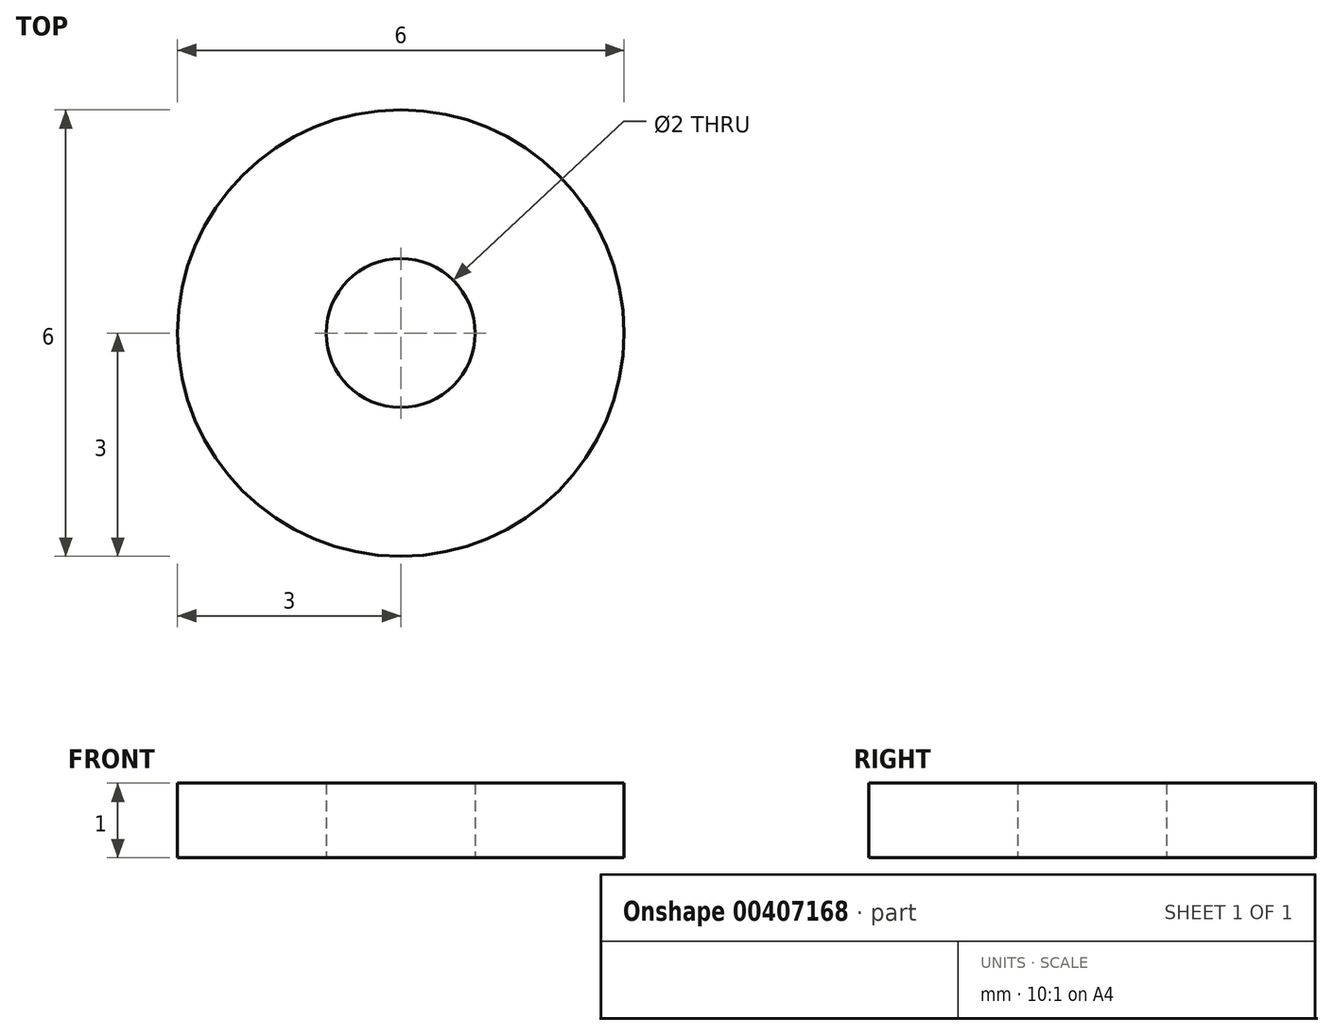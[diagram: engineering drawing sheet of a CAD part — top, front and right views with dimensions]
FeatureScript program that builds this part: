
annotation { "Feature Type Name" : "Feature", "Feature Type Description" : "" }
export const myFeature = defineFeature(function(context is Context, id is Id, definition is map)
    precondition{}
    {
        {
            var Q0;
            Q0=qCreatedBy(makeId("Top.planeOp"),FACE);
            var sketch = newSketch(context, id + "F0", { "sketchPlane" : qUnion([Q0])});
            skCircle(sketch, "E0", {"center": v(0, 0) * mm, "radius": 1 * mm});
            skCircle(sketch, "E1.0", {"center": v(0, 0) * mm, "radius": 3 * mm});
            skSolve(sketch);
        }
        {
            var Q0;
            Q0=makeQuery(id+"F0.imprint","IMPRINT",FACE,{"disambiguationData":[TD([[makeQuery(id+"F0.imprint","IMPRINT",EDGE,{"derivedFrom":sQuery(id+"F0.wireOp",EDGE,"E0")}),-1.0]])]});
            extrude(context, id + "F1", {"entities" : qUnion([Q0]), "depth" : 1 * mm});
        }
    });
